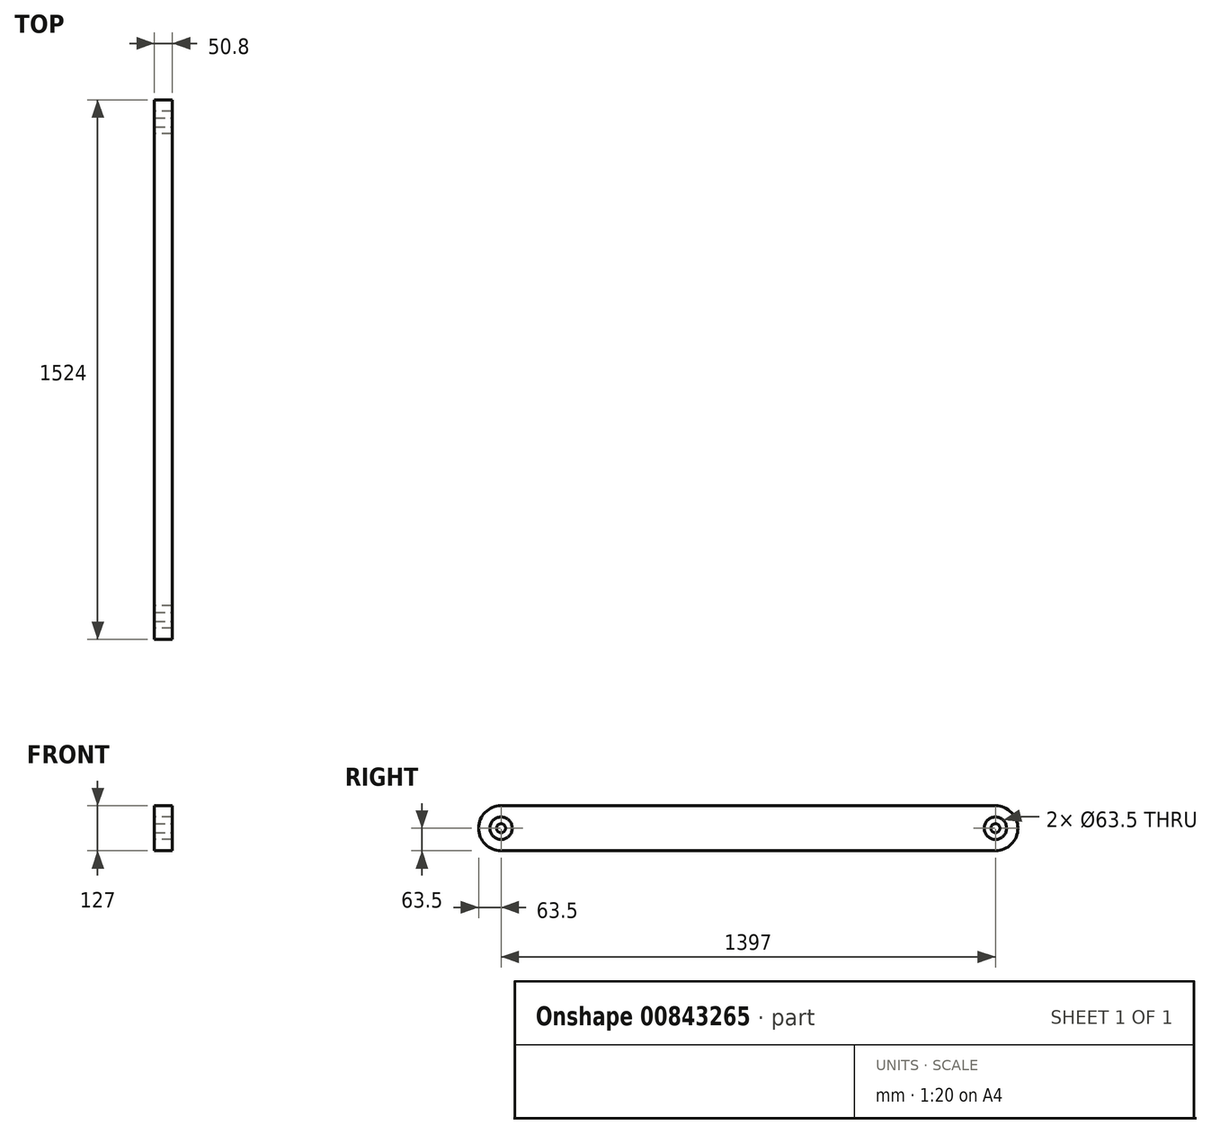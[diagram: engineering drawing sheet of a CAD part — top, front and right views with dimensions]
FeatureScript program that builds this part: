
annotation { "Feature Type Name" : "Feature", "Feature Type Description" : "" }
export const myFeature = defineFeature(function(context is Context, id is Id, definition is map)
    precondition{}
    {
        {
            var Q0;
            Q0=qCreatedBy(makeId("Right.planeOp"),FACE);
            var sketch = newSketch(context, id + "F0", { "sketchPlane" : qUnion([Q0])});
            skLineSegment(sketch, "E0.bottom", {"start": v(0, 0) * mm, "end": v(1397, 0) * mm});
            skLineSegment(sketch, "E0.top", {"start": v(0, 127) * mm, "end": v(1397, 127) * mm});
            skArc(sketch, "E1", {"start": v(0, 127) * mm, "mid": v(-63.5, 63.5) * mm, "end": v(0, 0) * mm});
            skArc(sketch, "E2", {"start": v(1397, 0) * mm, "mid": v(1460.5, 63.5) * mm, "end": v(1397, 127) * mm});
            skCircle(sketch, "E3", {"center": v(1397, 63.5) * mm, "radius": 31.75 * mm});
            skCircle(sketch, "E4", {"center": v(0, 63.5) * mm, "radius": 31.75 * mm});
            skSolve(sketch);
        }
        {
            var Q0;
            Q0=makeQuery(id+"F0.imprint","IMPRINT",FACE,{"disambiguationData":[TD([[makeQuery(id+"F0.imprint","IMPRINT",EDGE,{"derivedFrom":sQuery(id+"F0.wireOp",EDGE,"E0.bottom")}),1.0]])]});
            extrude(context, id + "F1", {"entities" : qUnion([Q0]), "depth" : 50.8 * mm, "offsetDistance" : 25.4 * mm});
        }
        {
            var Q0;
            Q0=makeQuery(id+"F1.opExtrude","CAP_FACE",FACE,{"disambiguationData":[OSD([sQuery(id+"F0.wireOp",EDGE,"E0.bottom"),sQuery(id+"F0.wireOp",EDGE,"E0.top"),sQuery(id+"F0.wireOp",EDGE,"E1"),sQuery(id+"F0.wireOp",EDGE,"E2"),sQuery(id+"F0.wireOp",EDGE,"E3"),sQuery(id+"F0.wireOp",EDGE,"E4")])],"isStart":false});
            var sketch = newSketch(context, id + "F2", { "sketchPlane" : qUnion([Q0])});
            skCircle(sketch, "E5", {"center": v(0, 63.5) * mm, "radius": 12.7 * mm});
            skCircle(sketch, "E6", {"center": v(1397, 63.5) * mm, "radius": 12.7 * mm});
            skSolve(sketch);
        }
        {
            var Q0;
            Q0 = qSketchRegion(id + "F2", true);
            extrude(context, id + "F3", {"entities" : qUnion([Q0]), "oppositeDirection" : true, "depth" : 50.8 * mm, "offsetDistance" : 25.4 * mm});
        }
    });
